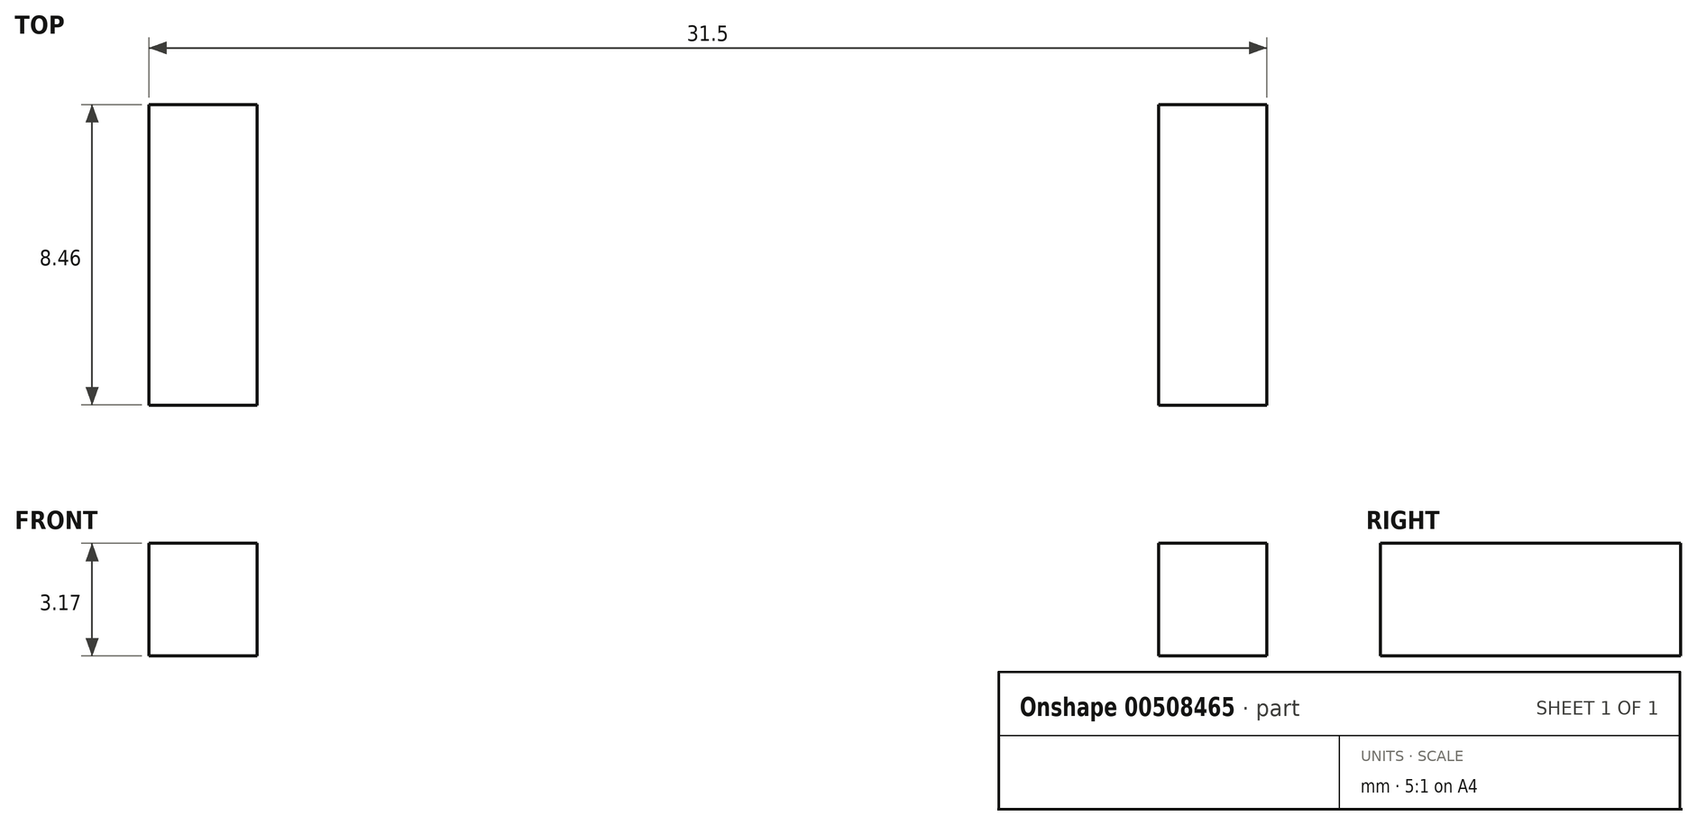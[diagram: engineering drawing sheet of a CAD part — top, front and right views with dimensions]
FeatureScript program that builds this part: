
annotation { "Feature Type Name" : "Feature", "Feature Type Description" : "" }
export const myFeature = defineFeature(function(context is Context, id is Id, definition is map)
    precondition{}
    {
        {
            var Q0;
            Q0=qCreatedBy(makeId("Top.planeOp"),FACE);
            var sketch = newSketch(context, id + "F0", { "sketchPlane" : qUnion([Q0])});
            skLineSegment(sketch, "E0.bottom", {"start": v(12.7, -12.7) * mm, "end": v(-12.7, -12.7) * mm});
            skLineSegment(sketch, "E0.top", {"start": v(12.7, 12.7) * mm, "end": v(-12.7, 12.7) * mm});
            skLineSegment(sketch, "E0.left", {"start": v(12.7, -12.7) * mm, "end": v(12.7, 12.7) * mm});
            skLineSegment(sketch, "E0.right", {"start": v(-12.7, -12.7) * mm, "end": v(-12.7, 12.7) * mm});
            skPoint(sketch, "E0.middle", {"position": v(0, 0) * mm});
            skLineSegment(sketch, "E1.bottom", {"start": v(-4.23, 12.7) * mm, "end": v(4.23, 12.7) * mm});
            skLineSegment(sketch, "E1.top", {"start": v(-4.23, 15.87) * mm, "end": v(4.23, 15.87) * mm});
            skLineSegment(sketch, "E1.left", {"start": v(-4.23, 12.7) * mm, "end": v(-4.23, 15.87) * mm});
            skLineSegment(sketch, "E1.right", {"start": v(4.23, 12.7) * mm, "end": v(4.23, 15.88) * mm});
            skLineSegment(sketch, "E2.bottom", {"start": v(12.7, 4.23) * mm, "end": v(15.75, 4.23) * mm});
            skLineSegment(sketch, "E2.top", {"start": v(12.7, -4.23) * mm, "end": v(15.75, -4.23) * mm});
            skLineSegment(sketch, "E2.left", {"start": v(12.7, 4.23) * mm, "end": v(12.7, -4.23) * mm});
            skLineSegment(sketch, "E2.right", {"start": v(15.75, 4.23) * mm, "end": v(15.75, -4.23) * mm});
            skLineSegment(sketch, "E3.bottom", {"start": v(-12.7, 4.23) * mm, "end": v(-15.75, 4.23) * mm});
            skLineSegment(sketch, "E3.top", {"start": v(-12.7, -4.23) * mm, "end": v(-15.75, -4.23) * mm});
            skLineSegment(sketch, "E3.left", {"start": v(-12.7, 4.23) * mm, "end": v(-12.7, -4.23) * mm});
            skLineSegment(sketch, "E3.right", {"start": v(-15.75, 4.23) * mm, "end": v(-15.75, -4.23) * mm});
            skLineSegment(sketch, "E4.bottom", {"start": v(-4.23, -12.7) * mm, "end": v(4.23, -12.7) * mm});
            skLineSegment(sketch, "E4.top", {"start": v(-4.23, -15.88) * mm, "end": v(4.23, -15.88) * mm});
            skLineSegment(sketch, "E4.left", {"start": v(-4.23, -12.7) * mm, "end": v(-4.23, -15.88) * mm});
            skLineSegment(sketch, "E4.right", {"start": v(4.23, -12.7) * mm, "end": v(4.23, -15.88) * mm});
            skSolve(sketch);
        }
        {
            var Q0;
            {var subQ0=sQuery(id+"F0.wireOp",EDGE,"E1.bottom");Q0=makeQuery(id+"F0.imprint","IMPRINT",FACE,{"disambiguationData":[TD([[makeQuery(id+"F0.imprint","IMPRINT",EDGE,{"derivedFrom":subQ0}),-1.0]])]});}
            var Q1;
            Q1=makeQuery(id+"F0.imprint","IMPRINT",FACE,{"disambiguationData":[TD([[makeQuery(id+"F0.imprint","IMPRINT",EDGE,{"derivedFrom":sQuery(id+"F0.wireOp",EDGE,"E3.bottom")}),1.0]])]});
            var Q2;
            Q2=makeQuery(id+"F0.imprint","IMPRINT",FACE,{"disambiguationData":[TD([[makeQuery(id+"F0.imprint","IMPRINT",EDGE,{"derivedFrom":sQuery(id+"F0.wireOp",EDGE,"E1.bottom")}),1.0]])]});
            var Q3;
            Q3=makeQuery(id+"F0.imprint","IMPRINT",FACE,{"disambiguationData":[TD([[makeQuery(id+"F0.imprint","IMPRINT",EDGE,{"derivedFrom":sQuery(id+"F0.wireOp",EDGE,"E2.bottom")}),-1.0]])]});
            var Q4;
            Q4=makeQuery(id+"F0.imprint","IMPRINT",FACE,{"disambiguationData":[TD([[makeQuery(id+"F0.imprint","IMPRINT",EDGE,{"derivedFrom":sQuery(id+"F0.wireOp",EDGE,"E4.bottom")}),-1.0]])]});
            extrude(context, id + "F1", {"entities" : qUnion([Q0, Q1, Q2, Q3, Q4]), "depth" : 3.17 * mm});
        }
    });
